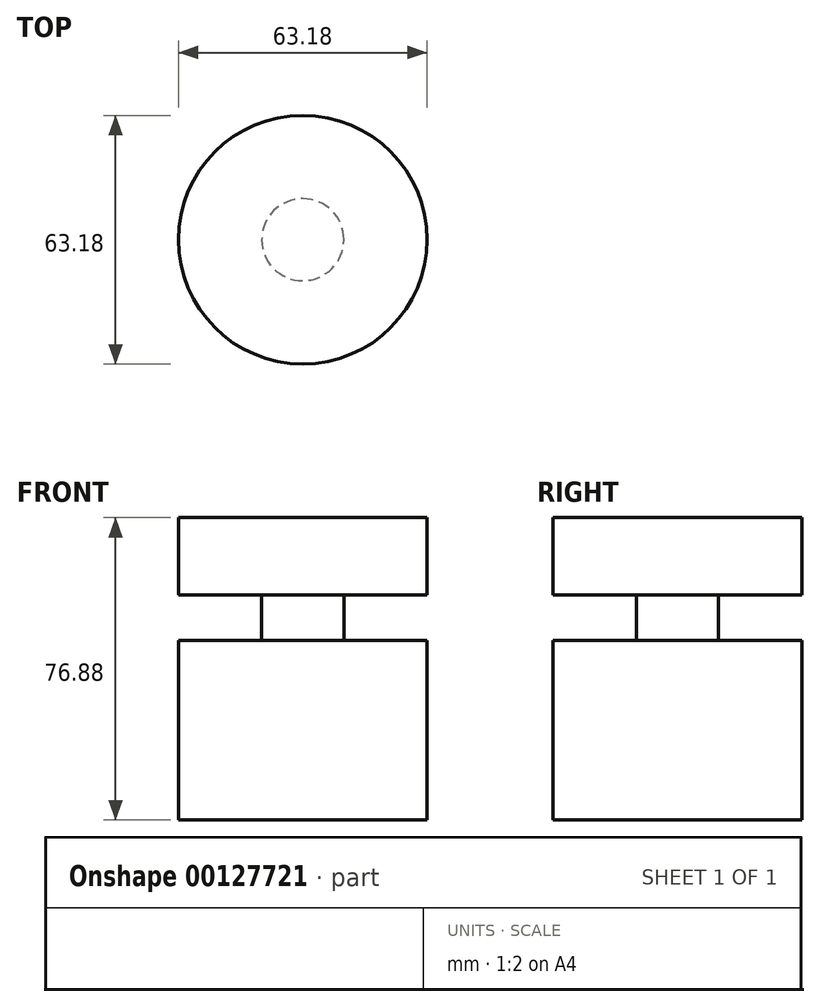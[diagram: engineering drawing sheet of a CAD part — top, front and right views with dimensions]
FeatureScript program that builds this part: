
annotation { "Feature Type Name" : "Feature", "Feature Type Description" : "" }
export const myFeature = defineFeature(function(context is Context, id is Id, definition is map)
    precondition{}
    {
        {
            var Q0;
            Q0=qCreatedBy(makeId("Right.planeOp"),FACE);
            var sketch = newSketch(context, id + "F0", { "sketchPlane" : qUnion([Q0])});
            skLineSegment(sketch, "E0", {"start": v(0, 39.19) * mm, "end": v(0, -38.59) * mm});
            skLineSegment(sketch, "E1", {"start": v(0, -38.59) * mm, "end": v(-31.59, -38.59) * mm});
            skLineSegment(sketch, "E2", {"start": v(-31.59, -38.59) * mm, "end": v(-31.59, 7) * mm});
            skLineSegment(sketch, "E3", {"start": v(-31.59, 7) * mm, "end": v(-10.43, 7) * mm});
            skLineSegment(sketch, "E4", {"start": v(-10.43, 7) * mm, "end": v(-10.43, 18.62) * mm});
            skLineSegment(sketch, "E5", {"start": v(-10.43, 18.62) * mm, "end": v(-31.59, 18.62) * mm});
            skLineSegment(sketch, "E6", {"start": v(-31.59, 18.62) * mm, "end": v(-31.59, 38.3) * mm});
            skLineSegment(sketch, "E7", {"start": v(-31.59, 38.3) * mm, "end": v(0, 38.3) * mm});
            skSolve(sketch);
        }
        {
            var Q0;
            Q0 = qSketchRegion(id + "F0", true);
            var Q1;
            Q1=sQuery(id+"F0.wireOp",EDGE,"E0");
            revolve(context, id + "F1", {"entities" : qUnion([Q0]), "axis" : qUnion([Q1]), "revolveType" : RevolveType.FULL});
        }
    });
